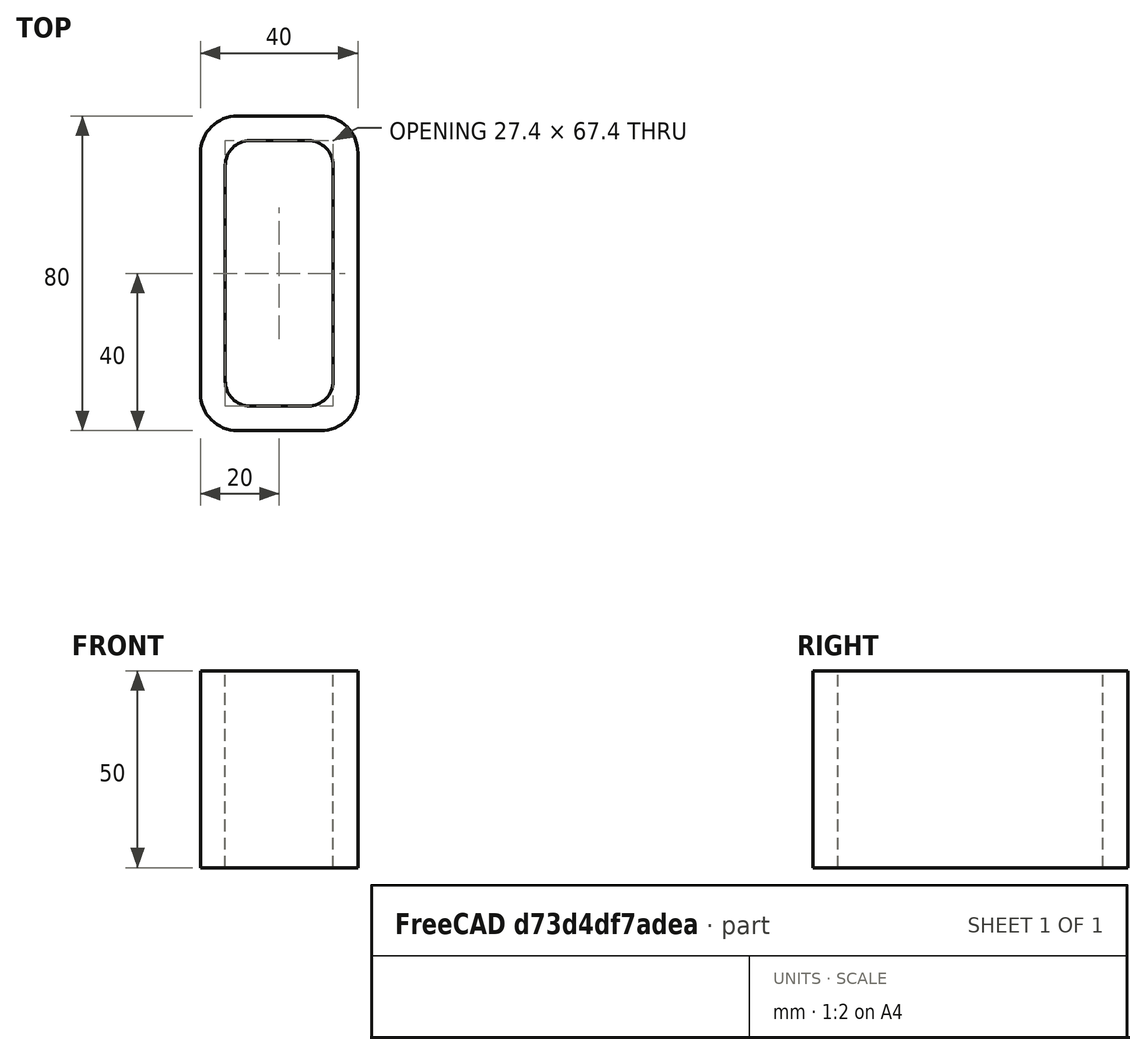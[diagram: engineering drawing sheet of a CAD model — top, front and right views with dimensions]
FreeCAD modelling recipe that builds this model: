
FCSTD DOCUMENT  (FreeCAD 0.15R4671 (Git))
Label: Rectangular hollow section 80x40x6.3 EN10219 S235JRH
License: All rights reserved
LicenseURL: http://en.wikipedia.org/wiki/All_rights_reserved
objects: Sketcher::SketchObject×1, Part::Extrusion×1
note: 2 computed .brp shape members not serialized (recipe doc carries the construction recipe); baked Part::Feature solids carry a one-line shape summary decoded from their .brp

FEATURE [Sketcher::SketchObject] Sketch
  sketch-geometry (16):
    g0: LineSegment StartX=-7.4 StartY=33.7 StartZ=0 EndX=7.4 EndY=33.7 EndZ=0
    g1: LineSegment StartX=13.7 StartY=27.4 StartZ=0 EndX=13.7 EndY=-27.4 EndZ=0
    g2: LineSegment StartX=7.4 StartY=-33.7 StartZ=0 EndX=-7.4 EndY=-33.7 EndZ=0
    g3: LineSegment StartX=-13.7 StartY=-27.4 StartZ=0 EndX=-13.7 EndY=27.4 EndZ=0
    g4: LineSegment StartX=-10.55 StartY=40 StartZ=0 EndX=10.55 EndY=40 EndZ=0
    g5: LineSegment StartX=20 StartY=30.55 StartZ=0 EndX=20 EndY=-30.55 EndZ=0
    g6: LineSegment StartX=10.55 StartY=-40 StartZ=0 EndX=-10.55 EndY=-40 EndZ=0
    g7: LineSegment StartX=-20 StartY=-30.55 StartZ=0 EndX=-20 EndY=30.55 EndZ=0
    g8: ArcOfCircle CenterX=-7.4 CenterY=27.4 CenterZ=0 NormalX=0 NormalY=0 NormalZ=1 Radius=6.3 StartAngle=1.5708 EndAngle=3.14159
    g9: ArcOfCircle CenterX=7.4 CenterY=27.4 CenterZ=0 NormalX=0 NormalY=0 NormalZ=1 Radius=6.3 StartAngle=0 EndAngle=1.5708
    g10: ArcOfCircle CenterX=7.4 CenterY=-27.4 CenterZ=0 NormalX=0 NormalY=0 NormalZ=1 Radius=6.3 StartAngle=4.71239 EndAngle=6.28319
    g11: ArcOfCircle CenterX=-7.4 CenterY=-27.4 CenterZ=0 NormalX=0 NormalY=0 NormalZ=1 Radius=6.3 StartAngle=3.14159 EndAngle=4.71239
    g12: ArcOfCircle CenterX=10.55 CenterY=30.55 CenterZ=0 NormalX=0 NormalY=0 NormalZ=1 Radius=9.45 StartAngle=0 EndAngle=1.5708
    g13: ArcOfCircle CenterX=10.55 CenterY=-30.55 CenterZ=0 NormalX=0 NormalY=0 NormalZ=1 Radius=9.45 StartAngle=4.71239 EndAngle=6.28319
    g14: ArcOfCircle CenterX=-10.55 CenterY=-30.55 CenterZ=0 NormalX=0 NormalY=0 NormalZ=1 Radius=9.45 StartAngle=3.14159 EndAngle=4.71239
    g15: ArcOfCircle CenterX=-10.55 CenterY=30.55 CenterZ=0 NormalX=0 NormalY=0 NormalZ=1 Radius=9.45 StartAngle=1.5708 EndAngle=3.14159
  constraints (36):
    c: Horizontal(g2)
    c: Vertical(g3)
    c: Horizontal(g6)
    c: Vertical(g7)
    c: Tangent(g3,g8) = 1.5708
    c: Tangent(g0,g8) = 1.5708
    c: Tangent(g0,g9) = 1.5708
    c: Tangent(g1,g9) = 1.5708
    c: Tangent(g1,g10) = 1.5708
    c: Tangent(g2,g10) = 1.5708
    c: Tangent(g2,g11) = 1.5708
    c: Tangent(g3,g11) = 1.5708
    c: Tangent(g4,g12) = 1.5708
    c: Tangent(g5,g12) = 1.5708
    c: Tangent(g5,g13) = 1.5708
    c: Tangent(g6,g13) = 1.5708
    c: Tangent(g6,g14) = 1.5708
    c: Tangent(g7,g14) = 1.5708
    c: Tangent(g7,g15) = 1.5708
    c: Tangent(g4,g15) = 1.5708
    c: Equal(g9,g8)
    c: Equal(g9,g11)
    c: Equal(g9,g10)
    c: Equal(g12,g15)
    c: Equal(g12,g14)
    c: Equal(g12,g13)
    c: Symmetric(g4,g6,g-1)
    c: Symmetric(g7,g5,g-2)
    c: DistanceY(g4,g6) = -80
    c: DistanceX(g7,g5) = 40
    c: Symmetric(g3,g1,g-2)
    c: Symmetric(g0,g2,g-1)
    c: DistanceY(g0,g4) = 6.3
    c: DistanceX(g5,g1) = -6.3
    c: Radius(g9) = 6.3
    c: Radius(g12) = 9.45
FEATURE [Part::Extrusion] Extrude  label="Rectangular hollow section 80x40x6.3 EN10219 S235JRH"
  Base = -> Sketch
  Dir = (0,0,50)
  Solid = true
